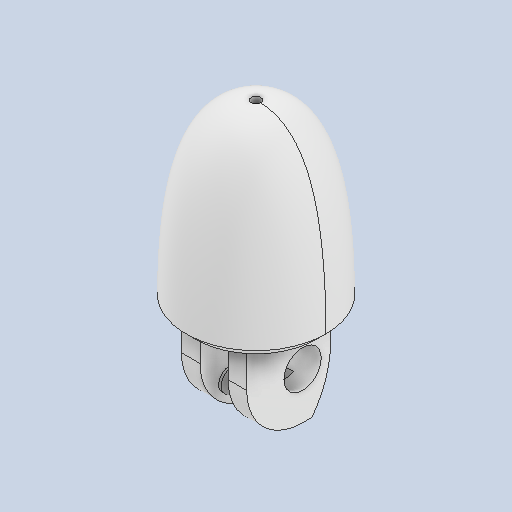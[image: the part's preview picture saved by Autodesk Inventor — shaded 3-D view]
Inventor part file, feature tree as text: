
AUTODESK INVENTOR PART (.ipt)
format: ipt  version: 2022 (Build 260153000, 153)  size: 279,552 bytes
history: native  units: in
note: dims shown in document units (in); Inventor stores cm internally (conversion verified against a paired STEP export)
features: sketch x7, extrude x5, fillet x4, chamfer x3, hole x1, plane x1, revolve x1
ambient origin geometry x8: Origin, YZ Plane, XZ Plane, XY Plane, X Axis, Y Axis, Z Axis, Center Point
bodies: Solid1 (feature_tree)
feature tree (22):
  extrude  "Extrusion1"  Depth=0.3937in
  fillet  "Fillet1"  Radius=0.3937in
  fillet  "Fillet2"  Radius=0.5906in
  extrude  "Extrusion2"  Depth=0.0394in TaperAngle=0.0deg
  chamfer  "Chamfer1"  Distance=0.0394in Angle=45.0deg
  fillet  "Fillet3"  Radius=0.0098in
  hole  "Hole1"  [1 undecoded]
  extrude  "Extrusion3"  Depth=0.0492in TaperAngle=0.0deg
  chamfer  "Chamfer2"  Distance=0.0492in Angle=45.0deg
  extrude  "Extrusion4"  TaperAngle=90.0deg  [1 undecoded]
  chamfer  "Chamfer3"  Distance=0.8937in
  plane  "Work Plane1"
  revolve  "Revolution1"  [1 undecoded]
  extrude  "Extrusion11"  Depth=0.0197in
  fillet  "Fillet4"  Radius=0.0344in
  sketch  "Sketch1"  dims[d8=0.3937in d9=0.0in d10=0.2362in d11=0.3937in d12=0.5906in]
  sketch  "Sketch2"  dims[d13=0.0984in d14=0.0394in d15=0.0in d16=0.0394in d17=0.0787in d18=45.0deg d19=0.0098in]
  sketch  "Sketch3"  dims[d20=0.1969in]
  sketch  "Sketch4"  dims[d21=0.1575in d22=0.2362in d23=0.1575in d24=0.0787in d25=90.0deg d26=0.3937in d27=0.0in d31=0.0591in d32=0.0in]
  sketch  "Sketch5"  dims[d33=0.0098in d34=0.0492in d35=45.0deg d36=0.0591in d37=0.0in d38=0.0098in d39=0.0492in d40=45.0deg]
  sketch  "Sketch12"  dims[d63=0.7087in d64=90.0deg]
  sketch  "Sketch13"  dims[d65=0.0394in d66=0.8937in d67=0.0in d68=0.0295in d52=0.0197in d53=0.0344in d54=0.0197in d55=0.0344in]
note: 3 required parameter values undecoded (feature->parameter linkage not recoverable at this tier; creation-order binding heuristic only, values carry confidence <= 0.55)